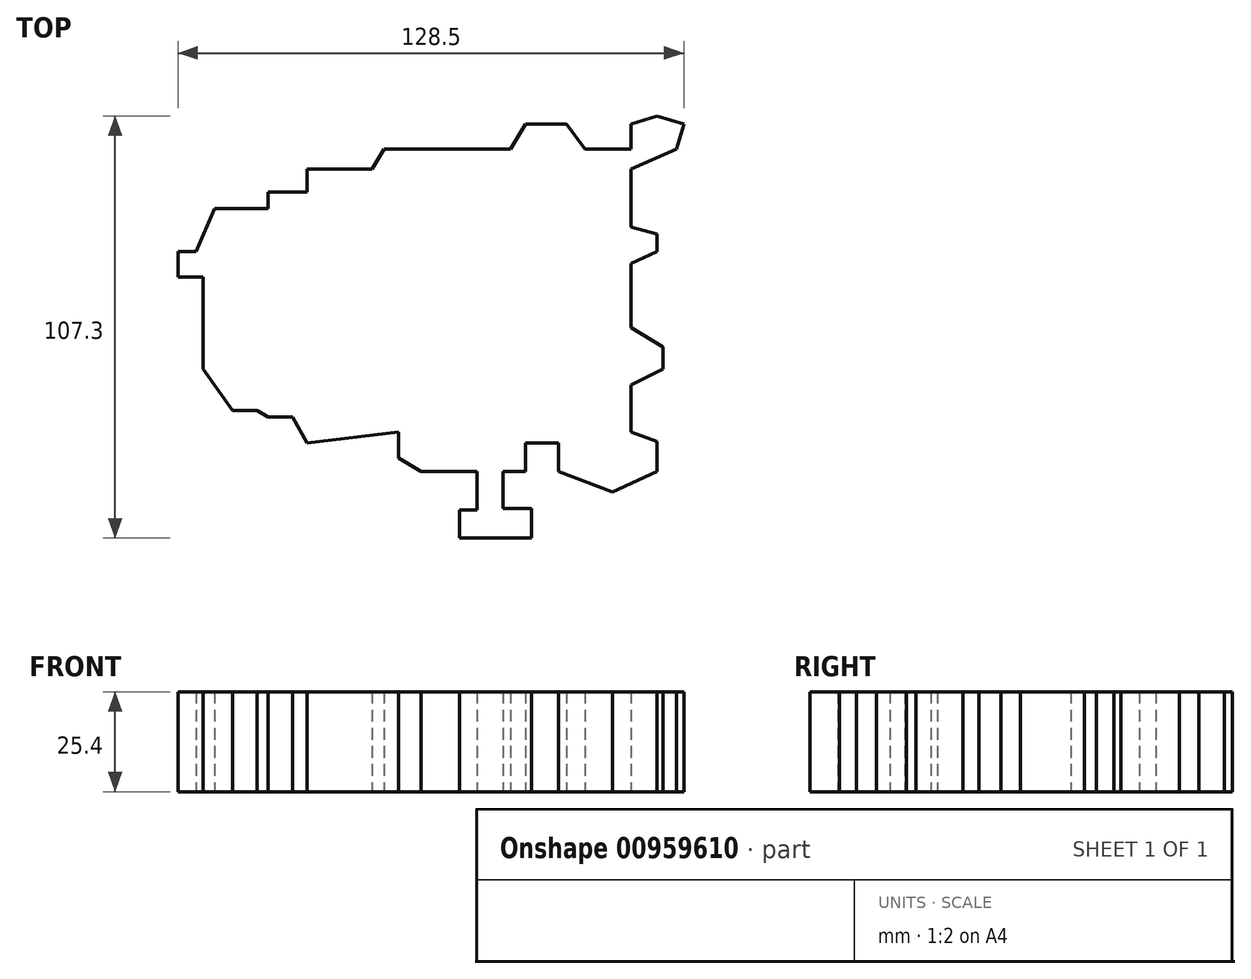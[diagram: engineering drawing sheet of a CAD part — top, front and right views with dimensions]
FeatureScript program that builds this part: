
annotation { "Feature Type Name" : "Feature", "Feature Type Description" : "" }
export const myFeature = defineFeature(function(context is Context, id is Id, definition is map)
    precondition{}
    {
        {
            var Q0;
            Q0=qCreatedBy(makeId("Top.planeOp"),FACE);
            var sketch = newSketch(context, id + "F0", { "sketchPlane" : qUnion([Q0])});
            skLineSegment(sketch, "E0", {"start": v(-51.71, -3.41) * mm, "end": v(-61.67, -3.41) * mm});
            skLineSegment(sketch, "E1", {"start": v(-61.67, -3.41) * mm, "end": v(-61.67, 0) * mm});
            skLineSegment(sketch, "E2", {"start": v(-61.67, 0) * mm, "end": v(-61.67, 3.04) * mm});
            skLineSegment(sketch, "E3", {"start": v(-61.67, 3.04) * mm, "end": v(-52.45, 3.04) * mm});
            skLineSegment(sketch, "E4", {"start": v(-52.45, 3.04) * mm, "end": v(-57.06, 3.04) * mm});
            skLineSegment(sketch, "E5", {"start": v(-57.06, 3.04) * mm, "end": v(-52.45, 13.92) * mm});
            skLineSegment(sketch, "E6", {"start": v(-52.45, 13.92) * mm, "end": v(-38.8, 13.92) * mm});
            skLineSegment(sketch, "E7", {"start": v(-38.8, 13.92) * mm, "end": v(-38.8, 18.16) * mm});
            skLineSegment(sketch, "E8", {"start": v(-38.8, 18.16) * mm, "end": v(-28.85, 18.16) * mm});
            skLineSegment(sketch, "E9", {"start": v(-28.85, 18.16) * mm, "end": v(-28.85, 24.06) * mm});
            skLineSegment(sketch, "E10", {"start": v(-28.85, 24.06) * mm, "end": v(-12.44, 24.06) * mm});
            skLineSegment(sketch, "E11", {"start": v(-12.44, 24.06) * mm, "end": v(-9.3, 29.04) * mm});
            skLineSegment(sketch, "E12", {"start": v(-9.3, 29.04) * mm, "end": v(22.77, 29.04) * mm});
            skLineSegment(sketch, "E13", {"start": v(22.77, 29.04) * mm, "end": v(26.64, 35.49) * mm});
            skLineSegment(sketch, "E14", {"start": v(26.64, 35.49) * mm, "end": v(36.96, 35.49) * mm});
            skLineSegment(sketch, "E15", {"start": v(36.96, 35.49) * mm, "end": v(41.76, 29.04) * mm});
            skLineSegment(sketch, "E16", {"start": v(41.76, 29.04) * mm, "end": v(53.37, 29.04) * mm});
            skLineSegment(sketch, "E17", {"start": v(53.37, 29.04) * mm, "end": v(53.37, 35.49) * mm});
            skLineSegment(sketch, "E18", {"start": v(53.37, 35.49) * mm, "end": v(60, 37.52) * mm});
            skLineSegment(sketch, "E19", {"start": v(60, 37.52) * mm, "end": v(66.83, 35.49) * mm});
            skLineSegment(sketch, "E20", {"start": v(66.83, 35.49) * mm, "end": v(64.91, 29.04) * mm});
            skLineSegment(sketch, "E21", {"start": v(64.91, 29.04) * mm, "end": v(53.37, 24.06) * mm});
            skLineSegment(sketch, "E22", {"start": v(53.37, 24.06) * mm, "end": v(53.37, 9.3) * mm});
            skLineSegment(sketch, "E23", {"start": v(53.37, 9.3) * mm, "end": v(60, 7.47) * mm});
            skLineSegment(sketch, "E24", {"start": v(60, 7.47) * mm, "end": v(60, 3.04) * mm});
            skLineSegment(sketch, "E25", {"start": v(60, 3.04) * mm, "end": v(53.37, 0) * mm});
            skLineSegment(sketch, "E26", {"start": v(53.37, 0) * mm, "end": v(53.37, -16.32) * mm});
            skLineSegment(sketch, "E27", {"start": v(53.37, -16.32) * mm, "end": v(61.56, -21.23) * mm});
            skLineSegment(sketch, "E28", {"start": v(61.56, -21.23) * mm, "end": v(61.56, -26.82) * mm});
            skLineSegment(sketch, "E29", {"start": v(61.56, -26.82) * mm, "end": v(53.37, -30.88) * mm});
            skLineSegment(sketch, "E30", {"start": v(53.37, -30.88) * mm, "end": v(53.37, -42.86) * mm});
            skLineSegment(sketch, "E31", {"start": v(53.37, -42.86) * mm, "end": v(60, -45.26) * mm});
            skLineSegment(sketch, "E32", {"start": v(60, -45.26) * mm, "end": v(60, -52.82) * mm});
            skLineSegment(sketch, "E33", {"start": v(60, -52.82) * mm, "end": v(48.76, -57.98) * mm});
            skLineSegment(sketch, "E34", {"start": v(48.76, -57.98) * mm, "end": v(34.94, -52.82) * mm});
            skLineSegment(sketch, "E35", {"start": v(34.94, -52.82) * mm, "end": v(34.94, -45.63) * mm});
            skLineSegment(sketch, "E36", {"start": v(34.94, -45.63) * mm, "end": v(26.64, -45.63) * mm});
            skLineSegment(sketch, "E37", {"start": v(26.64, -45.63) * mm, "end": v(26.64, -52.82) * mm});
            skLineSegment(sketch, "E38", {"start": v(26.64, -52.82) * mm, "end": v(20.92, -52.82) * mm});
            skLineSegment(sketch, "E39", {"start": v(20.92, -52.82) * mm, "end": v(20.92, -62.22) * mm});
            skLineSegment(sketch, "E40", {"start": v(20.92, -62.22) * mm, "end": v(28.11, -62.22) * mm});
            skLineSegment(sketch, "E41", {"start": v(28.11, -62.22) * mm, "end": v(28.11, -69.78) * mm});
            skLineSegment(sketch, "E42", {"start": v(28.11, -69.78) * mm, "end": v(9.86, -69.78) * mm});
            skLineSegment(sketch, "E43", {"start": v(9.86, -69.78) * mm, "end": v(9.86, -62.59) * mm});
            skLineSegment(sketch, "E44", {"start": v(9.86, -62.59) * mm, "end": v(14.29, -62.59) * mm});
            skLineSegment(sketch, "E45", {"start": v(14.29, -62.59) * mm, "end": v(14.29, -52.82) * mm});
            skLineSegment(sketch, "E46", {"start": v(14.29, -52.82) * mm, "end": v(0, -52.82) * mm});
            skLineSegment(sketch, "E47", {"start": v(0, -52.82) * mm, "end": v(-5.6, -49.46) * mm});
            skLineSegment(sketch, "E48", {"start": v(-5.6, -49.46) * mm, "end": v(-5.6, -42.86) * mm});
            skLineSegment(sketch, "E49", {"start": v(-5.6, -42.86) * mm, "end": v(-28.85, -45.63) * mm});
            skLineSegment(sketch, "E50", {"start": v(-28.85, -45.63) * mm, "end": v(-32.54, -39) * mm});
            skLineSegment(sketch, "E51", {"start": v(-32.54, -39) * mm, "end": v(-38.8, -39) * mm});
            skLineSegment(sketch, "E52", {"start": v(-38.8, -39) * mm, "end": v(-41.63, -37.3) * mm});
            skLineSegment(sketch, "E53", {"start": v(-41.63, -37.3) * mm, "end": v(-47.84, -37.3) * mm});
            skLineSegment(sketch, "E54", {"start": v(-47.84, -37.3) * mm, "end": v(-52.45, -30.88) * mm});
            skLineSegment(sketch, "E55", {"start": v(-52.45, -30.88) * mm, "end": v(-55.36, -26.82) * mm});
            skLineSegment(sketch, "E56", {"start": v(-55.36, -26.82) * mm, "end": v(-55.36, -3.41) * mm});
            skSolve(sketch);
        }
        {
            var Q0;
            {var subQ0=sQuery(id+"F0.wireOp",EDGE,"E1");Q0=makeQuery(id+"F0.imprint","IMPRINT",FACE,{"disambiguationData":[TD([[makeQuery(id+"F0.imprint","IMPRINT",EDGE,{"derivedFrom":subQ0}),-1.0]])]});}
            extrude(context, id + "F1", {"entities" : qUnion([Q0]), "depth" : 25.4 * mm, "offsetDistance" : 25.4 * mm});
        }
    });
